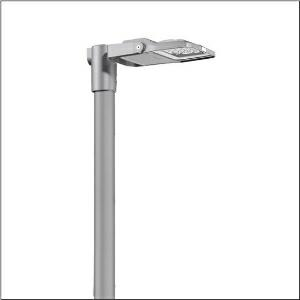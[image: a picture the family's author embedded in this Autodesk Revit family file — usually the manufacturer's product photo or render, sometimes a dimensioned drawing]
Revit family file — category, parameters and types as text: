
# Revit family: floodlight_fl_21_micro___pl33t_5xa7762a4f3a_891c
name_source: partatom
category: Lighting Fixtures
units: mm (PartAtom-declared; Revit-internal decimal feet)

## family parameters
Cut with Voids When Loaded = No
Host = Face
Light Source = No
Part Type = Normal
Room Calculation Point = No
Round Connector Dimension = Use Diameter
Shared = No

## types (1)
- --- (1 x LED, 3050 lm, 23.1 W, 4000K)
    Apparent Load = 23 VA
    CIE Flux Codes = 26 75 99 100 100
    Color Rendering = 70
    Color Temperature = 4000K
    Default Elevation = 1800 mm
    Description = Floodlight FL 21 micro, floodlight, primary light control with lens, of PMMA, primary optical cover: protective disc, of toughened safety glass, transparent, light distribution: PL33T, light emission: direct distribution, installation type: surface-mounted, LED, High Power LED, rated luminous flux: 3.050lm, luminous efficacy: 132lm/W, light colour: 740, colour temperature: 4000K, control gear: ECG iQ, control: Auto-Match, Temp-Guard, Night-Set, Smart-Wire, Desk-Remote (wireless, voltage-free reading and setting of iQ features in the workshop via application-optimized NFC function/RFID function), optimised constant luminous flux control (CLO 2.0), Street-Remote, with terminal, 6-pole, mains connection: 220..240V, AC, 50/60Hz, start of lifetime: 23W, end of lifetime: 24W, reduction: 11W, luminaire housing, of diecast aluminium, powder-coated, Siteco® metallic grey (DB 702S), corrosivity category C5 according to DIN EN ISO 12944, mast bracket, of steel, galvanised, powder-coated, Siteco® metallic grey (DB 702S), protection rating (complete): IP66, insulation class (complete): insulation class II (safety insulation), certification: CE, protection symbol: D, impact resistance: IK07, permissible operating ambient temperature: -40..+40°C, permissible operating ambient temperature for outdoor applications: -40..+50°C, standard: DIN EN 12944, packaging unit: 1 piece

Light Distribution: PL33T
    Height = 65 mm
    Lamp = 1 x LED
    Lamp Light Flux = 3050 lm
    Lamp Power = 23.1 W
    Lamp count = 1
    Length = 312 mm
    Luminous efficacy = 132 lm/W
    Manufacturer = Siteco
    ModVariant = No
    Model = 5XA7762A4F3A
    Number of Poles = 1
    OnlyDefault = Yes
    Power Factor = 1
    Product Name = Floodlight FL 21 micro | PL33T
    Product group = floodlight | pylon top
    ProductGroupID = 6101
    Protection Class = Protection class II
    Protection Degree = IP 66
    RLX_Detail_Level = 1
    RlxData = <blob elided: 101453 chars, md5=c222c165>
    Socket = socket
    Standby Power = 0 W
    System Light Flux = 3050 lm
    System Power = 23 W
    Type Comments = factory setting: luminous flux: 100 % | dim-lin: 254 | 455 mA
    Type Image = l_1007121.jpg
    URL = http://relux.com
    VarID = @adj_057955
    Voltage = 0 V
    Weight = 0.00 kg
    Width = 230 mm

## geometry (parser evidence)
native form markers: Blend x4, Sweep x10
no freeform markers — native parametric forms only
